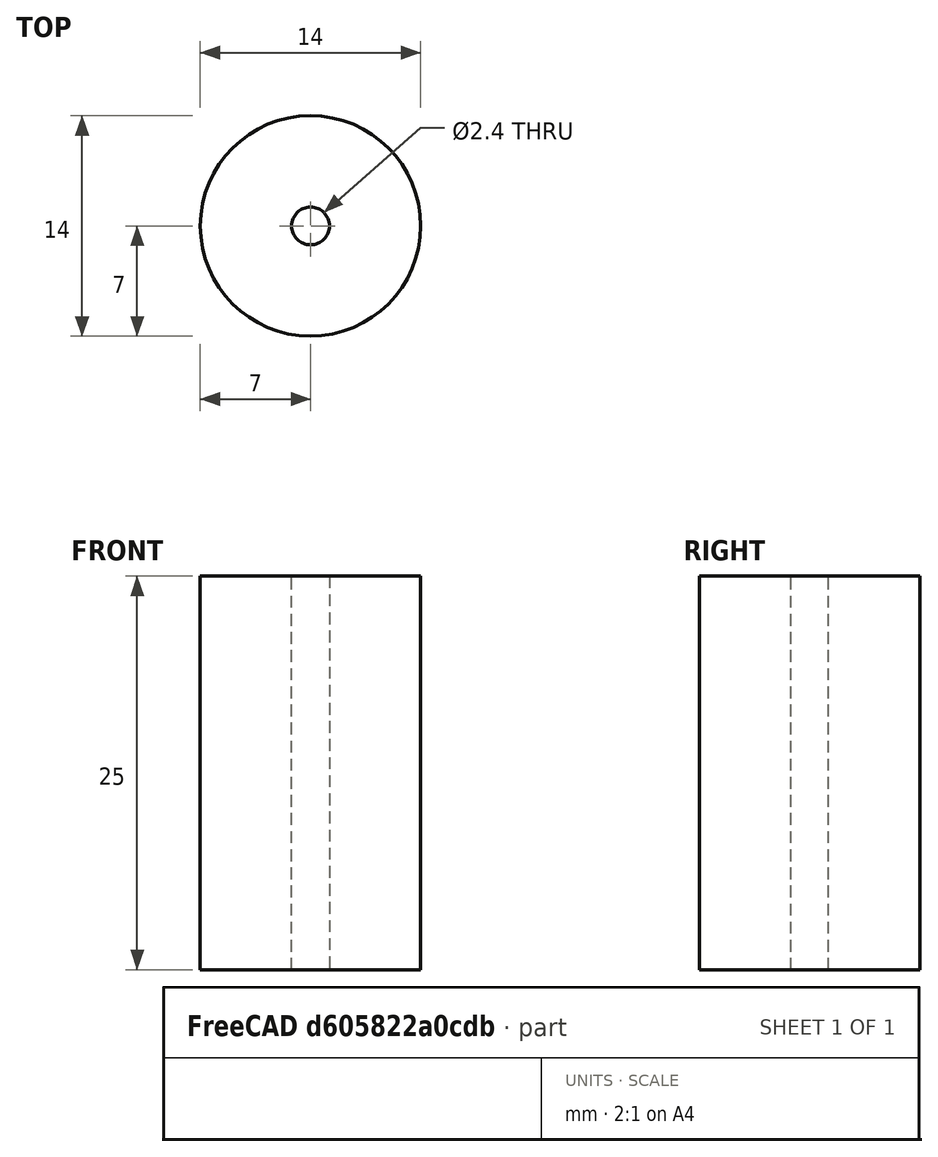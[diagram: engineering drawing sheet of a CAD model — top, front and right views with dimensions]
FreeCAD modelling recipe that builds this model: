
FCSTD DOCUMENT  (FreeCAD 0.21R33668 +26 (Git))
Label: arduino_connector
License: All rights reserved
LicenseURL: https://en.wikipedia.org/wiki/All_rights_reserved
objects: Sketcher::SketchObject×2, PartDesign::Pad×1, PartDesign::Pocket×1, PartDesign::Body×1
note: 7 computed .brp shape members not serialized (recipe doc carries the construction recipe); baked Part::Feature solids carry a one-line shape summary decoded from their .brp

FEATURE [Sketcher::SketchObject] Sketch
  FullyConstrained = false
  MapMode = 5
  Support = -> [XY_Plane]
  sketch-geometry (2):
    g0: Circle CenterX=0 CenterY=0 CenterZ=0 NormalX=0 NormalY=0 NormalZ=1 AngleXU=0 Radius=7
    g1: GeomPoint X=-3.90843 Y=5.80725 Z=0
  constraints (3):
    c: Coincident(g0,g-1)
    c: PointOnObject(g1,g0)
    c: Distance(g1,g0) = 7
FEATURE [PartDesign::Pad] Pad
  Direction = (0,0,1)
  Length = 25
  Length2 = 10
  Profile = -> Sketch
  ReferenceAxis = -> Sketch [N_Axis]
  Type = 0
FEATURE [Sketcher::SketchObject] Sketch001
  FullyConstrained = false
  MapMode = 5
  Placement = pos=(0,0,25) rot=(0,0,1;0rad)
  Support = -> [Pad]
  sketch-geometry (2):
    g0: Circle CenterX=0 CenterY=0 CenterZ=0 NormalX=0 NormalY=0 NormalZ=1 AngleXU=0 Radius=1.2
    g1: GeomPoint X=-0.940143 Y=0.745742 Z=0
  constraints (3):
    c: Coincident(g0,g-1)
    c: PointOnObject(g1,g0)
    c: Distance(g1,g0) = 1.2
FEATURE [PartDesign::Pocket] Pocket
  BaseFeature = -> Pad
  Direction = (0,0,-1)
  Length = 25
  Length2 = 5
  Profile = -> Sketch001
  ReferenceAxis = -> Sketch001 [N_Axis]
  Type = 0
FEATURE [PartDesign::Body] Body
  Group = -> [Sketch,Pad,Sketch001,Pocket]
  Origin = -> Origin
  Tip = -> Pocket
